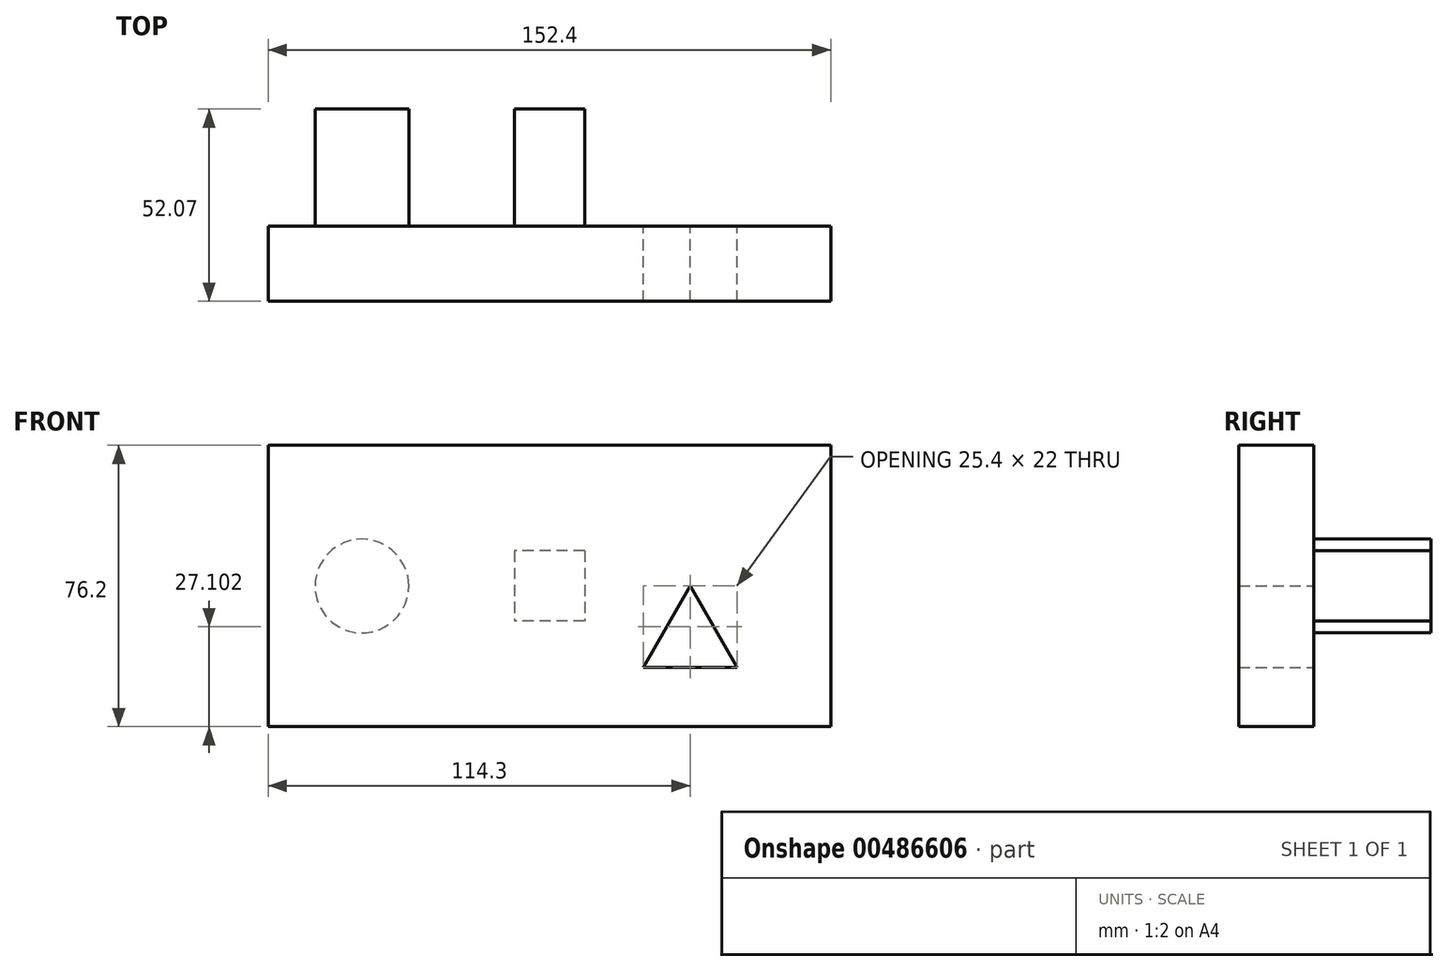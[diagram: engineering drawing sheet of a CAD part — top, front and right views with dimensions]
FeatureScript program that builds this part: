
annotation { "Feature Type Name" : "Feature", "Feature Type Description" : "" }
export const myFeature = defineFeature(function(context is Context, id is Id, definition is map)
    precondition{}
    {
        {
            var Q0;
            Q0=qCreatedBy(makeId("Front.planeOp"),FACE);
            var sketch = newSketch(context, id + "F0", { "sketchPlane" : qUnion([Q0])});
            skPoint(sketch, "E0.middle", {"position": v(0, 0) * mm});
            skLineSegment(sketch, "E1", {"start": v(0, 0) * mm, "end": v(-31.75, 0) * mm});
            skLineSegment(sketch, "E2.bottom", {"start": v(-22.22, 9.53) * mm, "end": v(-41.27, 9.53) * mm});
            skLineSegment(sketch, "E2.top", {"start": v(-22.22, -9.53) * mm, "end": v(-41.27, -9.52) * mm});
            skLineSegment(sketch, "E2.left", {"start": v(-22.22, 9.53) * mm, "end": v(-22.22, -9.53) * mm});
            skLineSegment(sketch, "E2.right", {"start": v(-41.27, 9.53) * mm, "end": v(-41.27, -9.52) * mm});
            skPoint(sketch, "E2.middle", {"position": v(-31.75, 0) * mm});
            skLineSegment(sketch, "E3", {"start": v(-31.75, 0) * mm, "end": v(-82.55, 0) * mm});
            skCircle(sketch, "E4", {"center": v(-82.55, 0) * mm, "radius": 12.7 * mm});
            skLineSegment(sketch, "E5", {"start": v(0, 0) * mm, "end": v(6.35, 0) * mm});
            skLineSegment(sketch, "E6", {"start": v(6.35, 0) * mm, "end": v(-6.35, -22) * mm});
            skLineSegment(sketch, "E7", {"start": v(-6.35, -22) * mm, "end": v(19.05, -22) * mm});
            skLineSegment(sketch, "E8", {"start": v(19.05, -22) * mm, "end": v(6.35, 0) * mm});
            skLineSegment(sketch, "E9.bottom", {"start": v(44.45, 38.1) * mm, "end": v(-107.95, 38.1) * mm});
            skLineSegment(sketch, "E9.top", {"start": v(44.45, -38.1) * mm, "end": v(-107.95, -38.1) * mm});
            skLineSegment(sketch, "E9.left", {"start": v(44.45, 38.1) * mm, "end": v(44.45, -38.1) * mm});
            skLineSegment(sketch, "E9.right", {"start": v(-107.95, 38.1) * mm, "end": v(-107.95, -38.1) * mm});
            skSolve(sketch);
        }
        {
            var Q0;
            Q0=makeQuery(id+"F0.imprint","IMPRINT",FACE,{"disambiguationData":[TD([[makeQuery(id+"F0.imprint","IMPRINT",EDGE,{"derivedFrom":sQuery(id+"F0.wireOp",EDGE,"E4")}),1.0]])]});
            var Q1;
            {var subQ1=sQuery(id+"F0.wireOp",EDGE,"E2.bottom");Q1=makeQuery(id+"F0.imprint","IMPRINT",FACE,{"disambiguationData":[TD([[makeQuery(id+"F0.imprint","IMPRINT",EDGE,{"derivedFrom":subQ1}),1.0]])]});}
            var Q2;
            {var subQ3=sQuery(id+"F0.wireOp",EDGE,"E2.bottom");Q2=makeQuery(id+"F0.imprint","IMPRINT",FACE,{"disambiguationData":[TD([[makeQuery(id+"F0.imprint","IMPRINT",EDGE,{"derivedFrom":subQ3}),-1.0]])]});}
            var Q3;
            {var subQ1=sQuery(id+"F0.wireOp",EDGE,"E2.top");Q3=makeQuery(id+"F0.imprint","IMPRINT",FACE,{"disambiguationData":[TD([[makeQuery(id+"F0.imprint","IMPRINT",EDGE,{"derivedFrom":subQ1}),-1.0]])]});}
            extrude(context, id + "F1", {"entities" : qUnion([Q0, Q1, Q2, Q3]), "depth" : 20.32 * mm});
        }
        {
            var Q0;
            Q0=makeQuery(id+"F0.imprint","IMPRINT",FACE,{"disambiguationData":[TD([[makeQuery(id+"F0.imprint","IMPRINT",EDGE,{"derivedFrom":sQuery(id+"F0.wireOp",EDGE,"E4")}),1.0]])]});
            var Q1;
            {var subQ1=sQuery(id+"F0.wireOp",EDGE,"E2.bottom");Q1=makeQuery(id+"F0.imprint","IMPRINT",FACE,{"disambiguationData":[TD([[makeQuery(id+"F0.imprint","IMPRINT",EDGE,{"derivedFrom":subQ1}),1.0]])]});}
            var Q2;
            {var subQ1=sQuery(id+"F0.wireOp",EDGE,"E2.top");Q2=makeQuery(id+"F0.imprint","IMPRINT",FACE,{"disambiguationData":[TD([[makeQuery(id+"F0.imprint","IMPRINT",EDGE,{"derivedFrom":subQ1}),-1.0]])]});}
            extrude(context, id + "F2", {"entities" : qUnion([Q0, Q1, Q2]), "operationType" : NewBodyOperationType.ADD, "oppositeDirection" : true, "depth" : 31.75 * mm});
        }
    });
